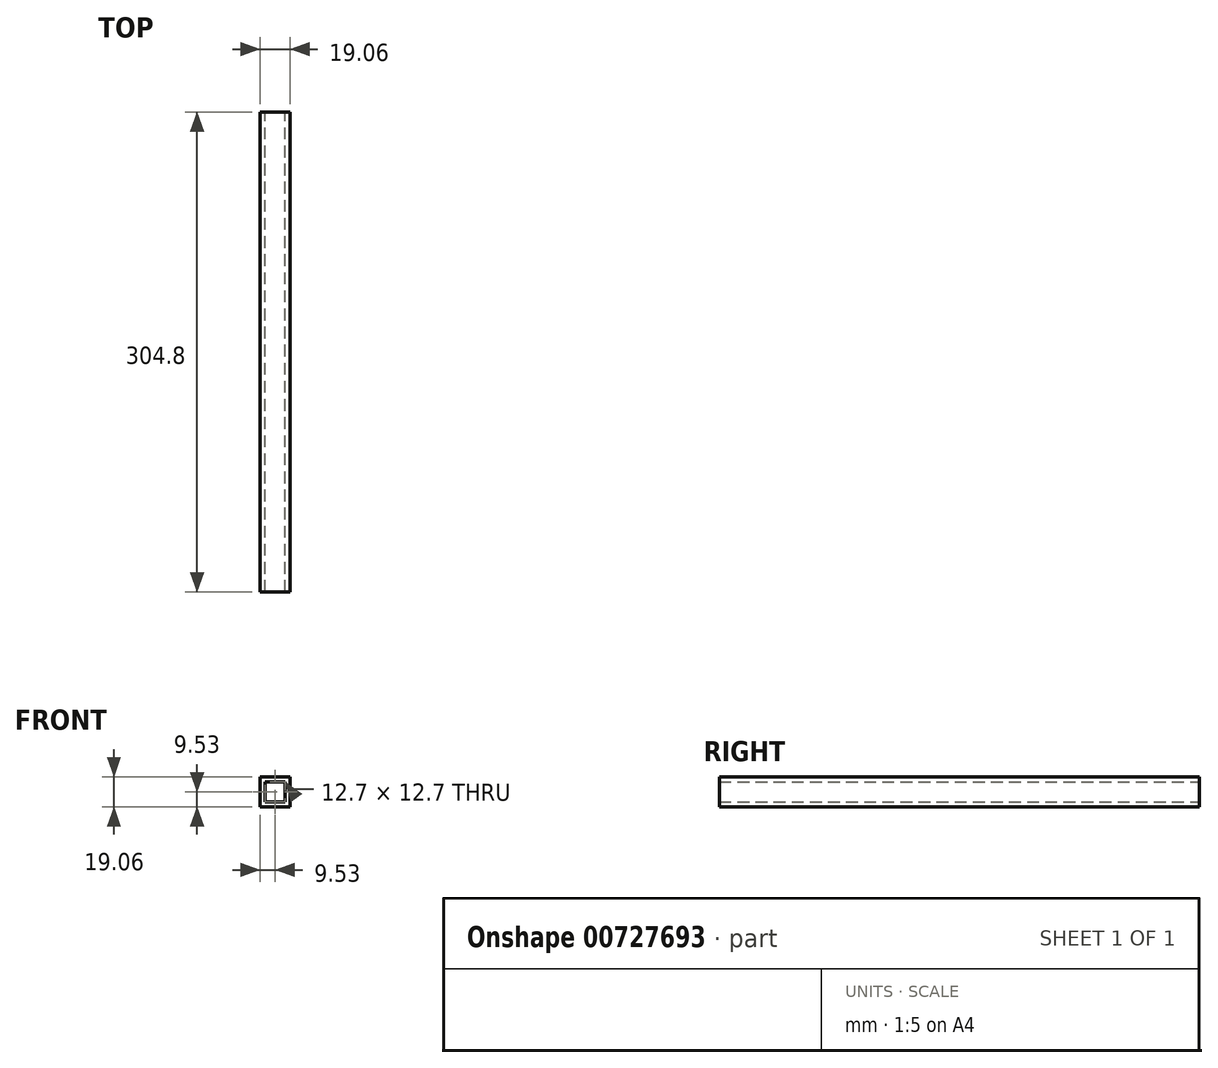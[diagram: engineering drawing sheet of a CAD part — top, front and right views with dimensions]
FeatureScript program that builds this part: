
annotation { "Feature Type Name" : "Feature", "Feature Type Description" : "" }
export const myFeature = defineFeature(function(context is Context, id is Id, definition is map)
    precondition{}
    {
        {
            var Q0;
            Q0=qCreatedBy(makeId("Front.planeOp"),FACE);
            var sketch = newSketch(context, id + "F0", { "sketchPlane" : qUnion([Q0])});
            skLineSegment(sketch, "E0.bottom", {"start": v(6.35, 6.35) * mm, "end": v(-6.35, 6.35) * mm});
            skLineSegment(sketch, "E0.top", {"start": v(6.35, -6.35) * mm, "end": v(-6.35, -6.35) * mm});
            skLineSegment(sketch, "E0.left", {"start": v(6.35, 6.35) * mm, "end": v(6.35, -6.35) * mm});
            skLineSegment(sketch, "E0.right", {"start": v(-6.35, 6.35) * mm, "end": v(-6.35, -6.35) * mm});
            skPoint(sketch, "E0.middle", {"position": v(0, 0) * mm});
            skLineSegment(sketch, "E1.0", {"start": v(9.53, -9.53) * mm, "end": v(-9.53, -9.53) * mm});
            skLineSegment(sketch, "E1.1", {"start": v(9.53, 9.53) * mm, "end": v(9.53, -9.53) * mm});
            skLineSegment(sketch, "E1.2", {"start": v(9.53, 9.53) * mm, "end": v(-9.53, 9.53) * mm});
            skLineSegment(sketch, "E1.3", {"start": v(-9.53, 9.53) * mm, "end": v(-9.53, -9.53) * mm});
            skSolve(sketch);
        }
        {
            var Q0;
            Q0 = qSketchRegion(id + "F0", true);
            extrude(context, id + "F1", {"entities" : qUnion([Q0]), "depth" : 304.8 * mm, "offsetDistance" : 25.4 * mm});
        }
    });
